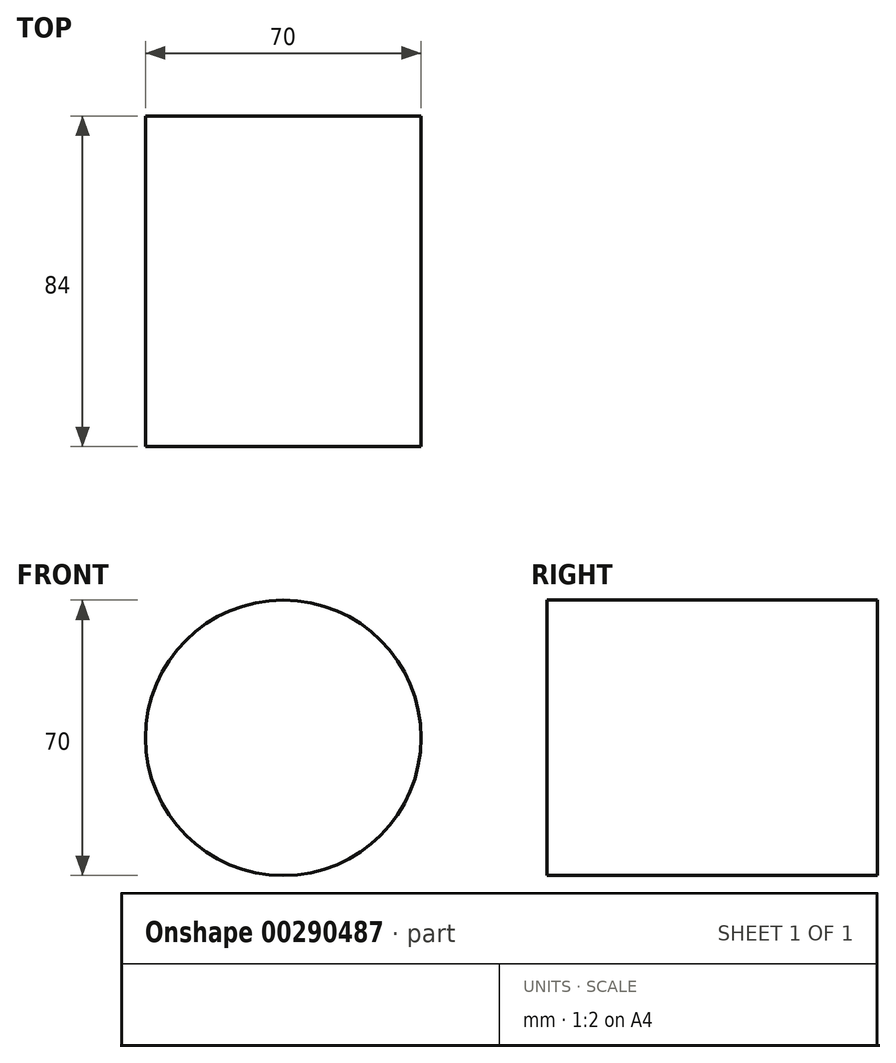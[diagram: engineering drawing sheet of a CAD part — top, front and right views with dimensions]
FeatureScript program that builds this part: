
annotation { "Feature Type Name" : "Feature", "Feature Type Description" : "" }
export const myFeature = defineFeature(function(context is Context, id is Id, definition is map)
    precondition{}
    {
        {
            var Q0;
            Q0=qCreatedBy(makeId("Front.planeOp"),FACE);
            var sketch = newSketch(context, id + "F0", { "sketchPlane" : qUnion([Q0])});
            skCircle(sketch, "E0", {"center": v(0, 0) * mm, "radius": 35 * mm});
            skSolve(sketch);
        }
        {
            var Q0;
            Q0 = qSketchRegion(id + "F0", true);
            extrude(context, id + "F1", {"entities" : qUnion([Q0]), "depth" : 84 * mm});
        }
    });
